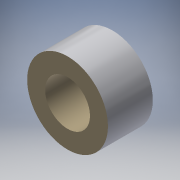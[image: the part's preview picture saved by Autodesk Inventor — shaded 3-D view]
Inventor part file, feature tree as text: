
AUTODESK INVENTOR PART (.ipt)
format: ipt  version: 2018 (Build 220112000, 112)  size: 106,496 bytes
history: native  units: in
note: dims shown in document units (in); Inventor stores cm internally (conversion verified against a paired STEP export)
features: extrude x1, sketch x1
ambient origin geometry x8: Origin, YZ Plane, XZ Plane, XY Plane, X Axis, Y Axis, Z Axis, Center Point
bodies: Solid1 (feature_tree)
feature tree (2):
  extrude  "Extrusion1"  Depth=0.1969in
  sketch  "Sketch1"  dims[d0=0.0787in d1=0.1969in d2=0.1969in d3=0.0in]
